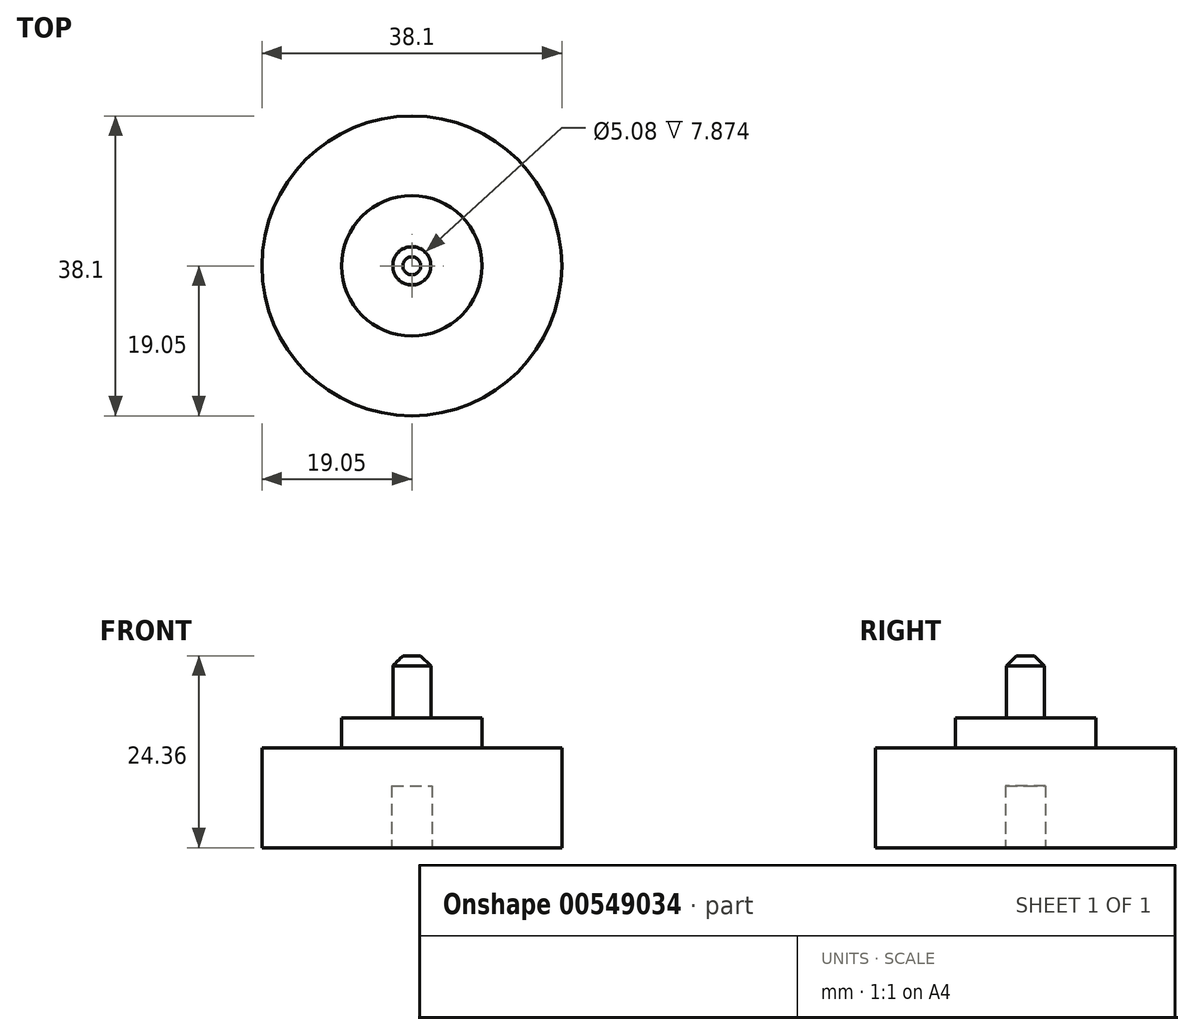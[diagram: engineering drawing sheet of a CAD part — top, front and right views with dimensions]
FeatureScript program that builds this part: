
annotation { "Feature Type Name" : "Feature", "Feature Type Description" : "" }
export const myFeature = defineFeature(function(context is Context, id is Id, definition is map)
    precondition{}
    {
        {
            var Q0;
            Q0=qCreatedBy(makeId("Front.planeOp"),FACE);
            var sketch = newSketch(context, id + "F0", { "sketchPlane" : qUnion([Q0])});
            skLineSegment(sketch, "E0", {"start": v(0, 0) * mm, "end": v(19.05, 0) * mm});
            skLineSegment(sketch, "E1", {"start": v(19.05, 0) * mm, "end": v(19.05, 12.7) * mm});
            skLineSegment(sketch, "E2", {"start": v(19.05, 12.7) * mm, "end": v(8.92, 12.7) * mm});
            skLineSegment(sketch, "E3", {"start": v(2.41, 16.5) * mm, "end": v(8.92, 16.5) * mm});
            skLineSegment(sketch, "E4", {"start": v(8.92, 16.5) * mm, "end": v(8.92, 12.7) * mm});
            skLineSegment(sketch, "E5", {"start": v(0, 24.36) * mm, "end": v(2.41, 24.36) * mm});
            skLineSegment(sketch, "E6", {"start": v(2.41, 24.36) * mm, "end": v(2.41, 16.5) * mm});
            skPoint(sketch, "E7.end.orphan", {"position": v(0, 16.5) * mm});
            skPoint(sketch, "E7.start.orphan", {"position": v(0, 12.7) * mm});
            skLineSegment(sketch, "E8", {"start": v(0, 0) * mm, "end": v(2.54, 0) * mm});
            skLineSegment(sketch, "E9", {"start": v(2.54, 0) * mm, "end": v(2.54, 7.87) * mm});
            skLineSegment(sketch, "E10", {"start": v(2.54, 7.87) * mm, "end": v(0, 7.87) * mm});
            skLineSegment(sketch, "E11", {"start": v(0, 7.87) * mm, "end": v(0, 24.36) * mm});
            skSolve(sketch);
        }
        {
            var Q0;
            Q0 = qSketchRegion(id + "F0", true);
            var Q1;
            Q1=sQuery(id+"F0.wireOp",EDGE,"E11");
            revolve(context, id + "F1", {"entities" : qUnion([Q0]), "axis" : qUnion([Q1]), "revolveType" : RevolveType.FULL});
        }
        {
            var Q0;
            Q0=makeQuery(id+"F1.opRevolve","SWEPT_EDGE",EDGE,{"disambiguationData":[OSD([sQuery(id+"F0.wireOp",EDGE,"E5"),sQuery(id+"F0.wireOp",EDGE,"E6")])]});
            chamfer(context, id + "F2", {"entities" : qUnion([Q0]), "width" : 1.27 * mm, "tangentPropagation" : true});
        }
    });
